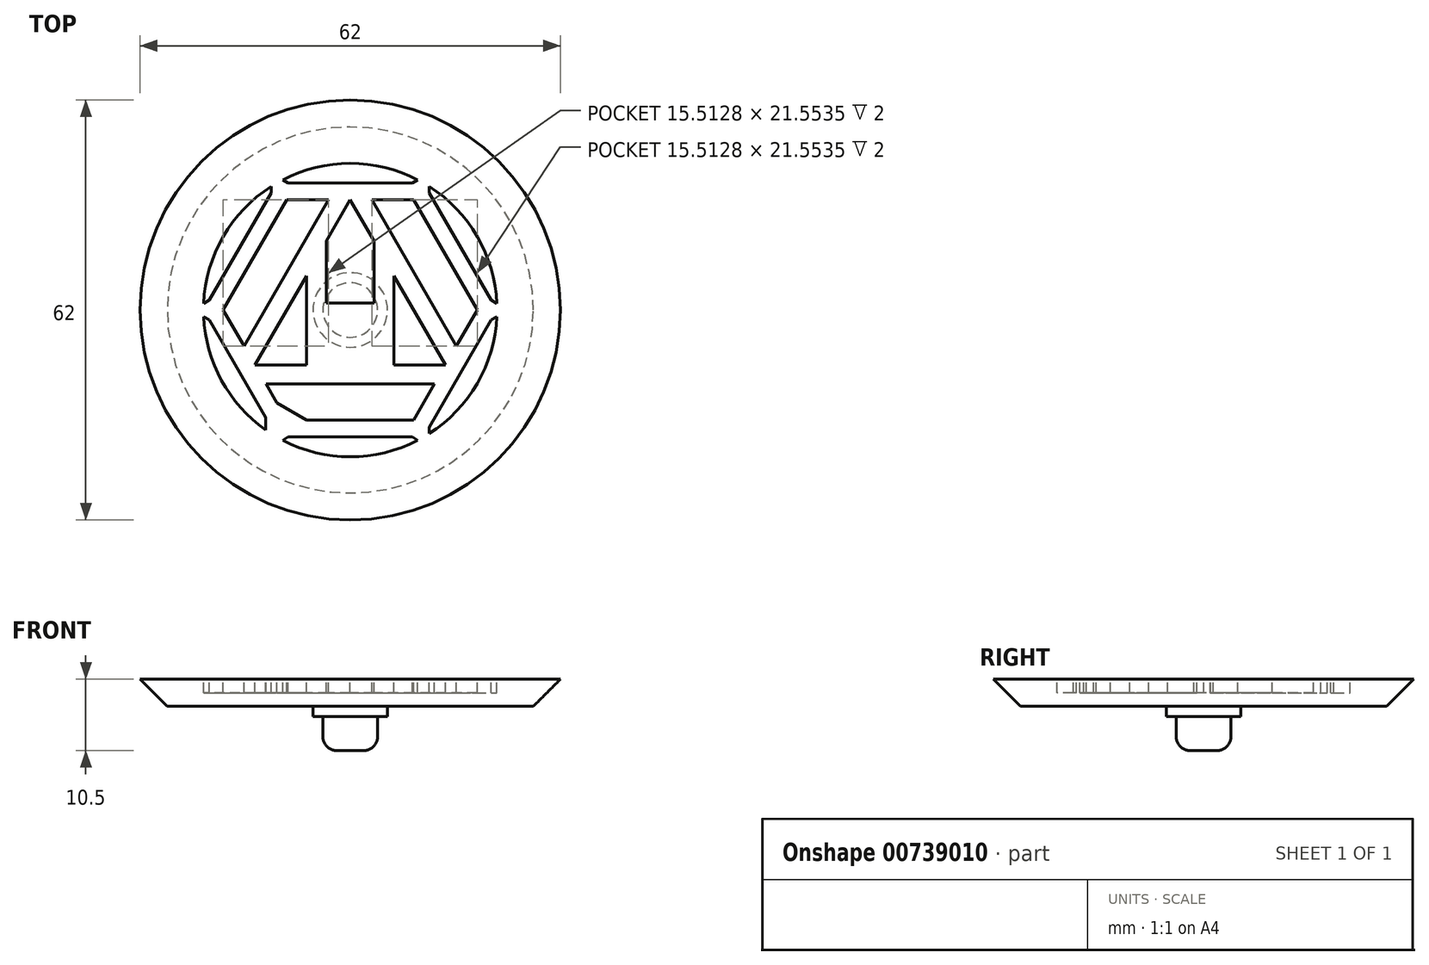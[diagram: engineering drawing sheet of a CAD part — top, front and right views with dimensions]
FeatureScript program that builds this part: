
annotation { "Feature Type Name" : "Feature", "Feature Type Description" : "" }
export const myFeature = defineFeature(function(context is Context, id is Id, definition is map)
    precondition{}
    {
        {
            var Q0;
            Q0=qCreatedBy(makeId("Top.planeOp"),FACE);
            var sketch = newSketch(context, id + "F0", { "sketchPlane" : qUnion([Q0])});
            skCircle(sketch, "E0", {"center": v(0, 0) * mm, "radius": 32 * mm});
            skSolve(sketch);
        }
        {
            var Q0;
            Q0=makeQuery(id+"F0.imprint","IMPRINT",FACE,{"disambiguationData":[TD([[makeQuery(id+"F0.imprint","IMPRINT",EDGE,{"derivedFrom":sQuery(id+"F0.wireOp",EDGE,"E0")}),1.0]])]});
            extrude(context, id + "F1", {"entities" : qUnion([Q0]), "depth" : 4 * mm, "offsetDistance" : 25 * mm});
        }
        {
            var Q0;
            Q0=makeQuery(id+"F1.opExtrude","CAP_EDGE",EDGE,{"disambiguationData":[OSD([sQuery(id+"F0.wireOp",EDGE,"E0")])],"isStart":true});
            chamfer(context, id + "F2", {"entities" : qUnion([Q0]), "width" : 5 * mm, "tangentPropagation" : true});
        }
        {
            var Q0;
            Q0=makeQuery(id+"F1.opExtrude","CAP_FACE",FACE,{"disambiguationData":[OSD([sQuery(id+"F0.wireOp",EDGE,"E0")])],"isStart":true});
            var sketch = newSketch(context, id + "F3", { "sketchPlane" : qUnion([Q0])});
            skCircle(sketch, "E1", {"center": v(0, 0) * mm, "radius": 4.03 * mm});
            skCircle(sketch, "E2", {"center": v(0, 0) * mm, "radius": 5.5 * mm});
            skSolve(sketch);
        }
        {
            var Q0;
            Q0=makeQuery(id+"F3.imprint","IMPRINT",FACE,{"disambiguationData":[TD([[makeQuery(id+"F3.imprint","IMPRINT",EDGE,{"derivedFrom":sQuery(id+"F3.wireOp",EDGE,"E1")}),-1.0]])]});
            extrude(context, id + "F4", {"entities" : qUnion([Q0]), "operationType" : NewBodyOperationType.ADD, "depth" : 1.5 * mm, "offsetDistance" : 25 * mm});
        }
        {
            var Q0;
            Q0=makeQuery(id+"F3.imprint","IMPRINT",FACE,{"disambiguationData":[TD([[makeQuery(id+"F3.imprint","IMPRINT",EDGE,{"derivedFrom":sQuery(id+"F3.wireOp",EDGE,"E1")}),1.0]])]});
            extrude(context, id + "F5", {"entities" : qUnion([Q0]), "operationType" : NewBodyOperationType.ADD, "depth" : 6.5 * mm, "offsetDistance" : 25 * mm});
        }
        {
            var Q0;
            Q0=makeQuery(id+"F1.opExtrude","CAP_FACE",FACE,{"disambiguationData":[OSD([sQuery(id+"F0.wireOp",EDGE,"E0")])],"isStart":false});
            var sketch = newSketch(context, id + "F6", { "sketchPlane" : qUnion([Q0])});
            skCircle(sketch, "E3", {"center": v(0, 0) * mm, "radius": 25 * mm});
            skLineSegment(sketch, "E4", {"start": v(-12.5, 21.65) * mm, "end": v(-25, 0) * mm});
            skLineSegment(sketch, "E5", {"start": v(-25, 0) * mm, "end": v(-12.5, -21.65) * mm});
            skLineSegment(sketch, "E6", {"start": v(-12.5, -21.65) * mm, "end": v(12.5, -21.65) * mm});
            skLineSegment(sketch, "E7", {"start": v(12.5, -21.65) * mm, "end": v(25, 0) * mm});
            skLineSegment(sketch, "E8", {"start": v(25, 0) * mm, "end": v(12.5, 21.65) * mm});
            skLineSegment(sketch, "E9", {"start": v(12.5, 21.65) * mm, "end": v(-12.5, 21.65) * mm});
            skCircle(sketch, "E10", {"center": v(0, 0) * mm, "radius": 21.65 * mm});
            skLineSegment(sketch, "E11", {"start": v(-10.83, 18.75) * mm, "end": v(-21.65, 0) * mm});
            skLineSegment(sketch, "E12", {"start": v(-21.65, 0) * mm, "end": v(-10.83, -18.75) * mm});
            skLineSegment(sketch, "E13", {"start": v(-10.83, -18.75) * mm, "end": v(10.83, -18.75) * mm});
            skLineSegment(sketch, "E14", {"start": v(10.83, -18.75) * mm, "end": v(21.65, 0) * mm});
            skLineSegment(sketch, "E15", {"start": v(21.65, 0) * mm, "end": v(10.83, 18.75) * mm});
            skLineSegment(sketch, "E16", {"start": v(10.83, 18.75) * mm, "end": v(-10.83, 18.75) * mm});
            skLineSegment(sketch, "E17", {"start": v(-12.5, -15.85) * mm, "end": v(-12.5, -17.68) * mm});
            skLineSegment(sketch, "E18", {"start": v(12.5, -15.85) * mm, "end": v(12.5, -17.68) * mm});
            skLineSegment(sketch, "E19", {"start": v(-10.83, -18.75) * mm, "end": v(-12.5, -21.65) * mm});
            skLineSegment(sketch, "E20", {"start": v(10.83, -18.75) * mm, "end": v(12.5, -21.65) * mm});
            skLineSegment(sketch, "E21.MirrorCS", {"start": v(-7.48, -18.75) * mm, "end": v(-9.06, -19.66) * mm});
            skLineSegment(sketch, "E22.MirrorCS", {"start": v(7.48, -18.75) * mm, "end": v(9.06, -19.66) * mm});
            skLineSegment(sketch, "E23", {"start": v(0, 0) * mm, "end": v(-0.1, 0) * mm});
            skLineSegment(sketch, "E24.MirrorCS", {"start": v(-12.5, 15.85) * mm, "end": v(-12.5, 17.68) * mm});
            skLineSegment(sketch, "E25.MirrorCS", {"start": v(-7.48, 18.75) * mm, "end": v(-9.06, 19.66) * mm});
            skLineSegment(sketch, "E26.MirrorCS", {"start": v(7.48, 18.75) * mm, "end": v(9.06, 19.66) * mm});
            skLineSegment(sketch, "E27.MirrorCS", {"start": v(12.5, 15.85) * mm, "end": v(12.5, 17.68) * mm});
            skLineSegment(sketch, "E28", {"start": v(-18.75, -10.83) * mm, "end": v(-16.24, -9.38) * mm});
            skLineSegment(sketch, "E29", {"start": v(16.24, -9.38) * mm, "end": v(18.75, -10.83) * mm});
            skLineSegment(sketch, "E30.MirrorCS", {"start": v(-19.98, -2.9) * mm, "end": v(-21.56, -1.99) * mm});
            skLineSegment(sketch, "E31.MirrorCS", {"start": v(-19.98, 2.9) * mm, "end": v(-21.56, 1.99) * mm});
            skLineSegment(sketch, "E32.MirrorCS", {"start": v(19.98, 2.9) * mm, "end": v(21.56, 1.99) * mm});
            skLineSegment(sketch, "E33.MirrorCS", {"start": v(19.98, -2.9) * mm, "end": v(21.56, -1.99) * mm});
            skCircle(sketch, "E34", {"center": v(0, 0) * mm, "radius": 18.75 * mm});
            skLineSegment(sketch, "E35", {"start": v(-9.38, 16.24) * mm, "end": v(-18.75, 0) * mm});
            skLineSegment(sketch, "E36", {"start": v(-18.75, 0) * mm, "end": v(-9.38, -16.24) * mm});
            skLineSegment(sketch, "E37", {"start": v(-9.38, -16.24) * mm, "end": v(9.38, -16.24) * mm});
            skLineSegment(sketch, "E38", {"start": v(9.38, -16.24) * mm, "end": v(18.75, 0) * mm});
            skLineSegment(sketch, "E39", {"start": v(18.75, 0) * mm, "end": v(9.38, 16.24) * mm});
            skLineSegment(sketch, "E40", {"start": v(9.38, 16.24) * mm, "end": v(-9.38, 16.24) * mm});
            skLineSegment(sketch, "E41", {"start": v(-6.47, -16.24) * mm, "end": v(-9.38, -16.24) * mm});
            skLineSegment(sketch, "E42", {"start": v(-9.38, -16.24) * mm, "end": v(-10.83, -13.73) * mm});
            skLineSegment(sketch, "E43", {"start": v(-10.83, -13.73) * mm, "end": v(-6.47, -16.24) * mm});
            skLineSegment(sketch, "E44", {"start": v(0, -16.24) * mm, "end": v(0, -18.75) * mm});
            skLineSegment(sketch, "E45", {"start": v(-16.24, -9.38) * mm, "end": v(-14.06, -8.12) * mm});
            skLineSegment(sketch, "E46.MirrorCS", {"start": v(10.83, -13.73) * mm, "end": v(6.47, -16.24) * mm});
            skLineSegment(sketch, "E47.MirrorCS", {"start": v(-10.83, 13.73) * mm, "end": v(-6.47, 16.24) * mm});
            skLineSegment(sketch, "E48.MirrorCS", {"start": v(10.83, 13.73) * mm, "end": v(6.47, 16.24) * mm});
            skLineSegment(sketch, "E49.MirrorCS", {"start": v(-17.3, -2.51) * mm, "end": v(-17.3, 2.51) * mm});
            skLineSegment(sketch, "E50", {"start": v(0, 0) * mm, "end": v(0, 0.1) * mm});
            skLineSegment(sketch, "E51.MirrorCS", {"start": v(17.3, -2.51) * mm, "end": v(17.3, 2.51) * mm});
            skLineSegment(sketch, "E52", {"start": v(-14.06, -8.12) * mm, "end": v(14.06, -8.12) * mm});
            skLineSegment(sketch, "E53", {"start": v(14.06, -8.12) * mm, "end": v(0, 16.24) * mm});
            skLineSegment(sketch, "E54", {"start": v(0, 16.24) * mm, "end": v(-14.06, -8.12) * mm});
            skLineSegment(sketch, "E55", {"start": v(-6.47, 16.24) * mm, "end": v(0, 16.24) * mm});
            skLineSegment(sketch, "E56", {"start": v(-3.24, 16.24) * mm, "end": v(-15.68, -5.32) * mm});
            skLineSegment(sketch, "E57", {"start": v(0, 16.24) * mm, "end": v(6.47, 16.24) * mm});
            skLineSegment(sketch, "E58", {"start": v(3.24, 16.24) * mm, "end": v(15.68, -5.32) * mm});
            skLineSegment(sketch, "E59", {"start": v(-14.06, -8.12) * mm, "end": v(-10.83, -13.73) * mm});
            skLineSegment(sketch, "E60", {"start": v(-12.44, -10.92) * mm, "end": v(12.44, -10.92) * mm});
            skLineSegment(sketch, "E61", {"start": v(-12.5, -15.85) * mm, "end": v(-10.83, -18.75) * mm});
            skLineSegment(sketch, "E62", {"start": v(-11.66, -17.3) * mm, "end": v(-11.66, -18.24) * mm});
            skPoint(sketch, "E62.endSnap0", {"position": v(-11.66, -17.3) * mm});
            skLineSegment(sketch, "E63.MirrorCS", {"start": v(-9.15, -18.75) * mm, "end": v(-9.97, -19.22) * mm});
            skLineSegment(sketch, "E64.MirrorCS", {"start": v(11.66, -17.3) * mm, "end": v(11.66, -18.24) * mm});
            skLineSegment(sketch, "E65.MirrorCS", {"start": v(9.15, -18.75) * mm, "end": v(9.97, -19.22) * mm});
            skLineSegment(sketch, "E66.MirrorCS", {"start": v(-9.15, 18.75) * mm, "end": v(-9.97, 19.22) * mm});
            skLineSegment(sketch, "E67.MirrorCS", {"start": v(-11.66, 17.3) * mm, "end": v(-11.66, 18.24) * mm});
            skLineSegment(sketch, "E68.MirrorCS", {"start": v(9.15, 18.75) * mm, "end": v(9.97, 19.22) * mm});
            skLineSegment(sketch, "E69.MirrorCS", {"start": v(11.66, 17.3) * mm, "end": v(11.66, 18.24) * mm});
            skLineSegment(sketch, "E70.MirrorCS", {"start": v(-20.81, -1.45) * mm, "end": v(-21.63, -0.98) * mm});
            skLineSegment(sketch, "E71.MirrorCS", {"start": v(-20.81, 1.45) * mm, "end": v(-21.63, 0.98) * mm});
            skLineSegment(sketch, "E72.MirrorCS", {"start": v(20.81, 1.45) * mm, "end": v(21.63, 0.98) * mm});
            skLineSegment(sketch, "E73.MirrorCS", {"start": v(20.81, -1.45) * mm, "end": v(21.63, -0.98) * mm});
            skLineSegment(sketch, "E74", {"start": v(-7.03, 4.06) * mm, "end": v(0, 16.24) * mm});
            skLineSegment(sketch, "E75", {"start": v(0, 16.24) * mm, "end": v(7.03, 4.06) * mm});
            skLineSegment(sketch, "E76", {"start": v(-3.52, 10.15) * mm, "end": v(-3.52, -8.12) * mm});
            skLineSegment(sketch, "E77", {"start": v(-3.52, -8.12) * mm, "end": v(-6.47, -8.12) * mm});
            skLineSegment(sketch, "E78", {"start": v(-6.47, -8.12) * mm, "end": v(-6.47, 5.02) * mm});
            skLineSegment(sketch, "E79", {"start": v(-3.52, 0) * mm, "end": v(0, 0) * mm});
            skLineSegment(sketch, "E80", {"start": v(-3.52, -8.12) * mm, "end": v(-3.52, 0) * mm});
            skLineSegment(sketch, "E81", {"start": v(-3.52, -4.06) * mm, "end": v(-3.52, 0) * mm});
            skLineSegment(sketch, "E82", {"start": v(-3.52, -2.03) * mm, "end": v(-3.52, 0) * mm});
            skLineSegment(sketch, "E83", {"start": v(-3.52, -1.01) * mm, "end": v(0, -1.01) * mm});
            skLineSegment(sketch, "E84", {"start": v(6.47, 5.02) * mm, "end": v(6.47, -8.12) * mm});
            skLineSegment(sketch, "E85", {"start": v(3.52, 10.15) * mm, "end": v(3.52, -8.12) * mm});
            skLineSegment(sketch, "E86", {"start": v(-0.1, 0) * mm, "end": v(-3.52, 0) * mm});
            skLineSegment(sketch, "E87", {"start": v(0, -1.01) * mm, "end": v(3.52, -1.01) * mm});
            skLineSegment(sketch, "E88", {"start": v(0, 0) * mm, "end": v(3.52, 0) * mm});
            skLineSegment(sketch, "E89", {"start": v(3.52, -8.12) * mm, "end": v(3.52, 0) * mm});
            skLineSegment(sketch, "E90", {"start": v(3.52, -8.12) * mm, "end": v(3.52, -1.01) * mm});
            skLineSegment(sketch, "E91", {"start": v(3.52, 0) * mm, "end": v(3.52, -1.01) * mm});
            skLineSegment(sketch, "E92.MirrorCS", {"start": v(0, 1.01) * mm, "end": v(3.52, 1.01) * mm});
            skLineSegment(sketch, "E93.MirrorCS", {"start": v(-3.52, 1.01) * mm, "end": v(0, 1.01) * mm});
            skSolve(sketch);
        }
        {
            var Q0;
            {var subQ3=sQuery(id+"F6.wireOp",EDGE,"E47.MirrorCS");Q0=makeQuery(id+"F6.imprint","IMPRINT",FACE,{"disambiguationData":[TD([[makeQuery(id+"F6.imprint","IMPRINT",EDGE,{"derivedFrom":subQ3}),-1.0]])]});}
            var Q1;
            {var subQ3=sQuery(id+"F6.wireOp",EDGE,"E49.MirrorCS");Q1=makeQuery(id+"F6.imprint","IMPRINT",FACE,{"disambiguationData":[TD([[makeQuery(id+"F6.imprint","IMPRINT",EDGE,{"derivedFrom":subQ3}),1.0]])]});}
            var Q2;
            {var subQ3=sQuery(id+"F6.wireOp",EDGE,"E47.MirrorCS");Q2=makeQuery(id+"F6.imprint","IMPRINT",FACE,{"disambiguationData":[TD([[makeQuery(id+"F6.imprint","IMPRINT",EDGE,{"derivedFrom":subQ3}),1.0]])]});}
            var Q3;
            {var subQ2=sQuery(id+"F6.wireOp",EDGE,"E48.MirrorCS");Q3=makeQuery(id+"F6.imprint","IMPRINT",FACE,{"disambiguationData":[TD([[makeQuery(id+"F6.imprint","IMPRINT",EDGE,{"derivedFrom":subQ2}),1.0]])]});}
            var Q4;
            {var subQ7=sQuery(id+"F6.wireOp",EDGE,"E92.MirrorCS");Q4=makeQuery(id+"F6.imprint","IMPRINT",FACE,{"disambiguationData":[TD([[makeQuery(id+"F6.imprint","IMPRINT",EDGE,{"derivedFrom":subQ7}),1.0]])]});}
            var Q5;
            {var subQ3=sQuery(id+"F6.wireOp",EDGE,"E48.MirrorCS");Q5=makeQuery(id+"F6.imprint","IMPRINT",FACE,{"disambiguationData":[TD([[makeQuery(id+"F6.imprint","IMPRINT",EDGE,{"derivedFrom":subQ3}),-1.0]])]});}
            var Q6;
            {var subQ3=sQuery(id+"F6.wireOp",EDGE,"E51.MirrorCS");Q6=makeQuery(id+"F6.imprint","IMPRINT",FACE,{"disambiguationData":[TD([[makeQuery(id+"F6.imprint","IMPRINT",EDGE,{"derivedFrom":subQ3}),-1.0]])]});}
            var Q7;
            {var subQ0=sQuery(id+"F6.wireOp",EDGE,"E53");Q7=makeQuery(id+"F6.imprint","IMPRINT",FACE,{"disambiguationData":[TD([[makeQuery(id+"F6.imprint","IMPRINT",EDGE,{"derivedFrom":subQ0}),1.0]])]});}
            var Q8;
            {var subQ3=sQuery(id+"F6.wireOp",EDGE,"E43");Q8=makeQuery(id+"F6.imprint","IMPRINT",FACE,{"disambiguationData":[TD([[makeQuery(id+"F6.imprint","IMPRINT",EDGE,{"derivedFrom":subQ3}),1.0]])]});}
            var Q9;
            {var subQ3=sQuery(id+"F6.wireOp",EDGE,"E80");Q9=makeQuery(id+"F6.imprint","IMPRINT",FACE,{"disambiguationData":[TD([[makeQuery(id+"F6.imprint","IMPRINT",EDGE,{"derivedFrom":subQ3}),-1.0]])]});}
            var Q10;
            {var subQ0=sQuery(id+"F6.wireOp",EDGE,"E54");Q10=makeQuery(id+"F6.imprint","IMPRINT",FACE,{"disambiguationData":[TD([[makeQuery(id+"F6.imprint","IMPRINT",EDGE,{"derivedFrom":subQ0}),1.0]])]});}
            var Q11;
            Q11=makeQuery(id+"F6.imprint","IMPRINT",FACE,{"disambiguationData":[TD([[makeQuery(id+"F6.imprint","IMPRINT",EDGE,{"derivedFrom":sQuery(id+"F6.wireOp",EDGE,"E42")}),-1.0]])]});
            var Q12;
            {var subQ3=sQuery(id+"F6.wireOp",EDGE,"E46.MirrorCS");Q12=makeQuery(id+"F6.imprint","IMPRINT",FACE,{"disambiguationData":[TD([[makeQuery(id+"F6.imprint","IMPRINT",EDGE,{"derivedFrom":subQ3}),1.0]])]});}
            var Q13;
            {var subQ0=sQuery(id+"F6.wireOp",EDGE,"E17");Q13=makeQuery(id+"F6.imprint","IMPRINT",FACE,{"disambiguationData":[TD([[makeQuery(id+"F6.imprint","IMPRINT",EDGE,{"derivedFrom":subQ0}),-1.0]])]});}
            var Q14;
            {var subQ0=sQuery(id+"F6.wireOp",EDGE,"E28");Q14=makeQuery(id+"F6.imprint","IMPRINT",FACE,{"disambiguationData":[TD([[makeQuery(id+"F6.imprint","IMPRINT",EDGE,{"derivedFrom":subQ0}),1.0]])]});}
            var Q15;
            {var subQ0=sQuery(id+"F6.wireOp",EDGE,"E30.MirrorCS");Q15=makeQuery(id+"F6.imprint","IMPRINT",FACE,{"disambiguationData":[TD([[makeQuery(id+"F6.imprint","IMPRINT",EDGE,{"derivedFrom":subQ0}),-1.0]])]});}
            var Q16;
            {var subQ0=sQuery(id+"F6.wireOp",EDGE,"E31.MirrorCS");Q16=makeQuery(id+"F6.imprint","IMPRINT",FACE,{"disambiguationData":[TD([[makeQuery(id+"F6.imprint","IMPRINT",EDGE,{"derivedFrom":subQ0}),1.0]])]});}
            var Q17;
            {var subQ0=sQuery(id+"F6.wireOp",EDGE,"E24.MirrorCS");Q17=makeQuery(id+"F6.imprint","IMPRINT",FACE,{"disambiguationData":[TD([[makeQuery(id+"F6.imprint","IMPRINT",EDGE,{"derivedFrom":subQ0}),1.0]])]});}
            var Q18;
            {var subQ0=sQuery(id+"F6.wireOp",EDGE,"E24.MirrorCS");Q18=makeQuery(id+"F6.imprint","IMPRINT",FACE,{"disambiguationData":[TD([[makeQuery(id+"F6.imprint","IMPRINT",EDGE,{"derivedFrom":subQ0}),-1.0]])]});}
            var Q19;
            {var subQ0=sQuery(id+"F6.wireOp",EDGE,"E25.MirrorCS");Q19=makeQuery(id+"F6.imprint","IMPRINT",FACE,{"disambiguationData":[TD([[makeQuery(id+"F6.imprint","IMPRINT",EDGE,{"derivedFrom":subQ0}),-1.0]])]});}
            var Q20;
            {var subQ0=sQuery(id+"F6.wireOp",EDGE,"E25.MirrorCS");Q20=makeQuery(id+"F6.imprint","IMPRINT",FACE,{"disambiguationData":[TD([[makeQuery(id+"F6.imprint","IMPRINT",EDGE,{"derivedFrom":subQ0}),1.0]])]});}
            var Q21;
            {var subQ0=sQuery(id+"F6.wireOp",EDGE,"E26.MirrorCS");Q21=makeQuery(id+"F6.imprint","IMPRINT",FACE,{"disambiguationData":[TD([[makeQuery(id+"F6.imprint","IMPRINT",EDGE,{"derivedFrom":subQ0}),-1.0]])]});}
            var Q22;
            {var subQ0=sQuery(id+"F6.wireOp",EDGE,"E27.MirrorCS");Q22=makeQuery(id+"F6.imprint","IMPRINT",FACE,{"disambiguationData":[TD([[makeQuery(id+"F6.imprint","IMPRINT",EDGE,{"derivedFrom":subQ0}),1.0]])]});}
            var Q23;
            {var subQ0=sQuery(id+"F6.wireOp",EDGE,"E27.MirrorCS");Q23=makeQuery(id+"F6.imprint","IMPRINT",FACE,{"disambiguationData":[TD([[makeQuery(id+"F6.imprint","IMPRINT",EDGE,{"derivedFrom":subQ0}),-1.0]])]});}
            var Q24;
            {var subQ0=sQuery(id+"F6.wireOp",EDGE,"E32.MirrorCS");Q24=makeQuery(id+"F6.imprint","IMPRINT",FACE,{"disambiguationData":[TD([[makeQuery(id+"F6.imprint","IMPRINT",EDGE,{"derivedFrom":subQ0}),-1.0]])]});}
            var Q25;
            {var subQ0=sQuery(id+"F6.wireOp",EDGE,"E33.MirrorCS");Q25=makeQuery(id+"F6.imprint","IMPRINT",FACE,{"disambiguationData":[TD([[makeQuery(id+"F6.imprint","IMPRINT",EDGE,{"derivedFrom":subQ0}),1.0]])]});}
            var Q26;
            {var subQ0=sQuery(id+"F6.wireOp",EDGE,"E29");Q26=makeQuery(id+"F6.imprint","IMPRINT",FACE,{"disambiguationData":[TD([[makeQuery(id+"F6.imprint","IMPRINT",EDGE,{"derivedFrom":subQ0}),1.0]])]});}
            var Q27;
            {var subQ0=sQuery(id+"F6.wireOp",EDGE,"E18");Q27=makeQuery(id+"F6.imprint","IMPRINT",FACE,{"disambiguationData":[TD([[makeQuery(id+"F6.imprint","IMPRINT",EDGE,{"derivedFrom":subQ0}),1.0]])]});}
            var Q28;
            {var subQ0=sQuery(id+"F6.wireOp",EDGE,"E18");Q28=makeQuery(id+"F6.imprint","IMPRINT",FACE,{"disambiguationData":[TD([[makeQuery(id+"F6.imprint","IMPRINT",EDGE,{"derivedFrom":subQ0}),-1.0]])]});}
            var Q29;
            {var subQ0=sQuery(id+"F6.wireOp",EDGE,"E22.MirrorCS");Q29=makeQuery(id+"F6.imprint","IMPRINT",FACE,{"disambiguationData":[TD([[makeQuery(id+"F6.imprint","IMPRINT",EDGE,{"derivedFrom":subQ0}),1.0]])]});}
            var Q30;
            {var subQ5=sQuery(id+"F6.wireOp",EDGE,"E21.MirrorCS");Q30=makeQuery(id+"F6.imprint","IMPRINT",FACE,{"disambiguationData":[TD([[makeQuery(id+"F6.imprint","IMPRINT",EDGE,{"derivedFrom":subQ5}),1.0]])]});}
            var Q31;
            {var subQ0=sQuery(id+"F6.wireOp",EDGE,"E21.MirrorCS");Q31=makeQuery(id+"F6.imprint","IMPRINT",FACE,{"disambiguationData":[TD([[makeQuery(id+"F6.imprint","IMPRINT",EDGE,{"derivedFrom":subQ0}),-1.0]])]});}
            extrude(context, id + "F7", {"entities" : qUnion([Q0, Q1, Q2, Q3, Q4, Q5, Q6, Q7, Q8, Q9, Q10, Q11, Q12, Q13, Q14, Q15, Q16, Q17, Q18, Q19, Q20, Q21, Q22, Q23, Q24, Q25, Q26, Q27, Q28, Q29, Q30, Q31]), "operationType" : NewBodyOperationType.REMOVE, "oppositeDirection" : true, "depth" : 2 * mm, "offsetDistance" : 25 * mm});
        }
        {
            var Q0;
            Q0=makeQuery(id+"F5.opExtrude","CAP_EDGE",EDGE,{"disambiguationData":[OSD([sQuery(id+"F3.wireOp",EDGE,"E1")])],"isStart":false});
            fillet(context, id + "F8", {"entities" : qUnion([Q0]), "radius" : 2 * mm, "tangentPropagation" : true, "allowEdgeOverflow" : false});
        }
    });
